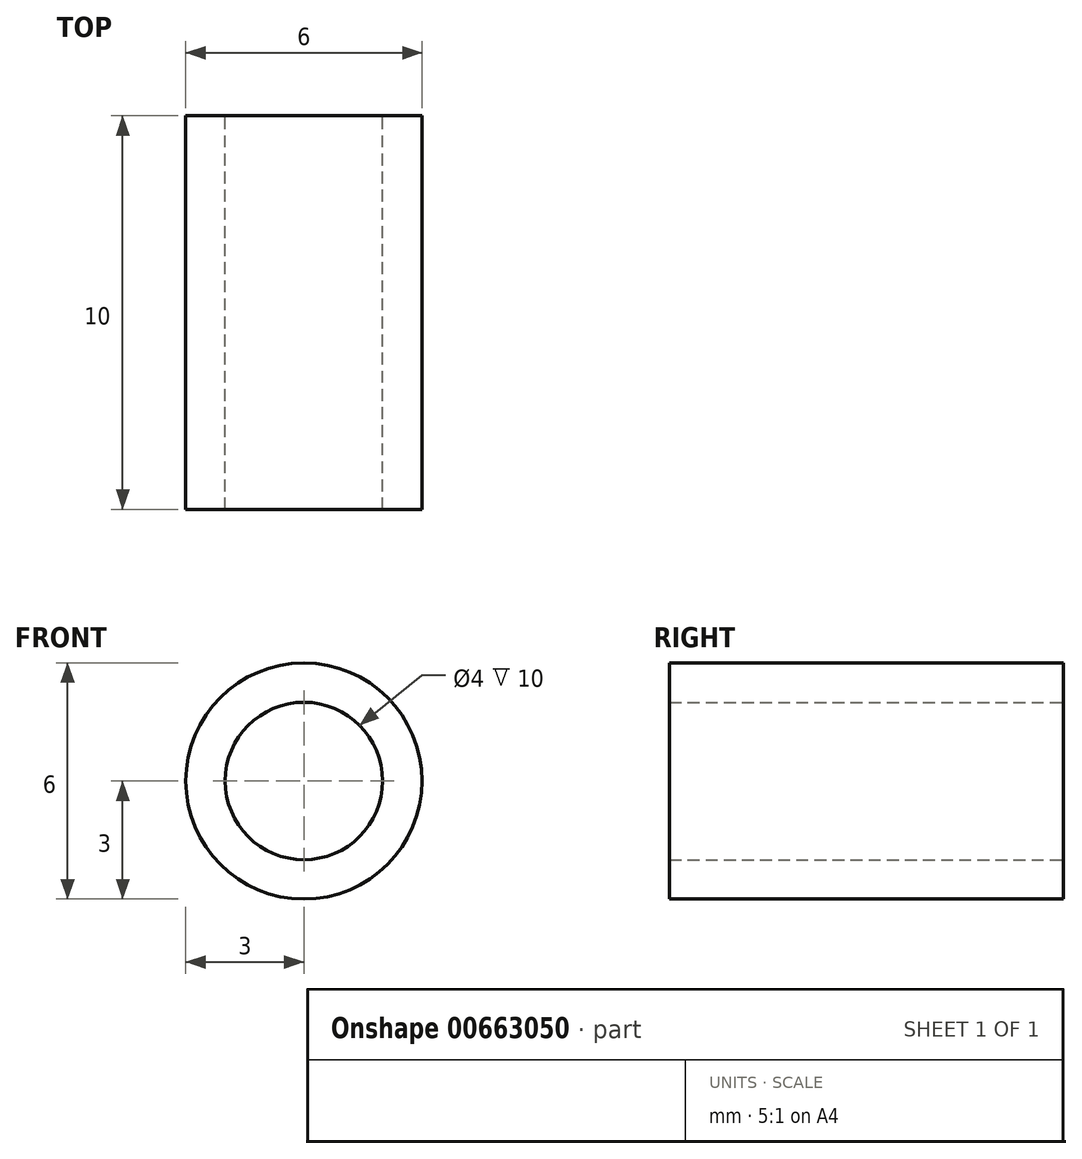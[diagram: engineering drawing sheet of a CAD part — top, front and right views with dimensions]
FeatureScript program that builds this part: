
annotation { "Feature Type Name" : "Feature", "Feature Type Description" : "" }
export const myFeature = defineFeature(function(context is Context, id is Id, definition is map)
    precondition{}
    {
        {
            var Q0;
            Q0=qCreatedBy(makeId("Front.planeOp"),FACE);
            var sketch = newSketch(context, id + "F0", { "sketchPlane" : qUnion([Q0])});
            skCircle(sketch, "E0", {"center": v(0, 0) * mm, "radius": 3 * mm});
            skCircle(sketch, "E1", {"center": v(0, 0) * mm, "radius": 2 * mm});
            skSolve(sketch);
        }
        {
            var Q0;
            Q0 = qSketchRegion(id + "F0", true);
            extrude(context, id + "F1", {"entities" : qUnion([Q0]), "depth" : 10 * mm, "offsetDistance" : 25 * mm});
        }
    });
